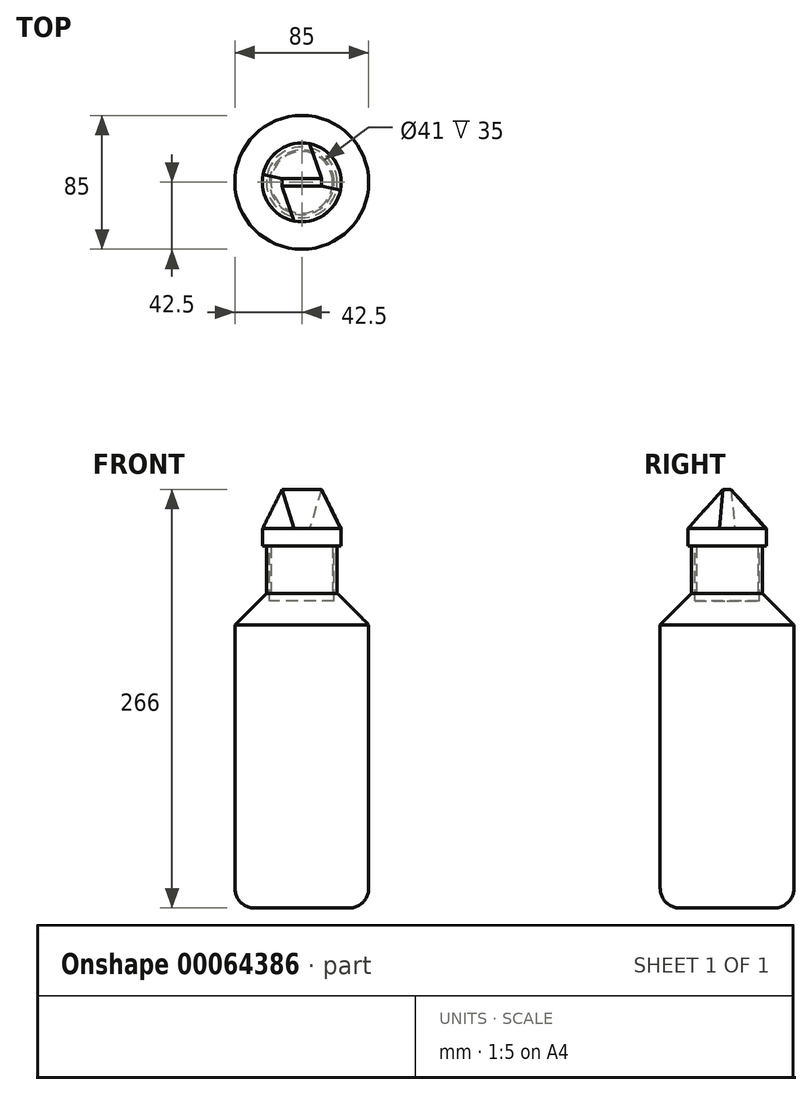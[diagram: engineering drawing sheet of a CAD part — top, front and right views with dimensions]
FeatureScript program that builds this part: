
annotation { "Feature Type Name" : "Feature", "Feature Type Description" : "" }
export const myFeature = defineFeature(function(context is Context, id is Id, definition is map)
    precondition{}
    {
        {
            var Q0;
            Q0=qCreatedBy(makeId("Top.planeOp"),FACE);
            var sketch = newSketch(context, id + "F0", { "sketchPlane" : qUnion([Q0])});
            skCircle(sketch, "E0", {"center": v(0, 0) * mm, "radius": 42.5 * mm});
            skSolve(sketch);
        }
        {
            var Q0;
            Q0 = qSketchRegion(id + "F0", true);
            extrude(context, id + "F1", {"entities" : qUnion([Q0]), "depth" : 180 * mm});
        }
        {
            var Q0;
            Q0=makeQuery(id+"F1.opExtrude","CAP_FACE",FACE,{"disambiguationData":[OSD([sQuery(id+"F0.wireOp",EDGE,"E0")])],"isStart":false});
            cPlane(context, id + "F2", {"entities" : qUnion([Q0]), "cplaneType" : CPlaneType.OFFSET, "offset" : 20 * mm, "width" : 152.4 * mm, "height" : 152.4 * mm});
        }
        {
            var Q0;
            Q0=qCreatedBy(id+"F2.planeOp",FACE);
            var sketch = newSketch(context, id + "F3", { "sketchPlane" : qUnion([Q0])});
            skCircle(sketch, "E1", {"center": v(0, 0) * mm, "radius": 22.5 * mm});
            skSolve(sketch);
        }
        {
            var Q1;
            Q1=makeQuery(id+"F1.opExtrude","CAP_FACE",FACE,{"disambiguationData":[OSD([sQuery(id+"F0.wireOp",EDGE,"E0")])],"isStart":false});
            var Q2;
            Q2=makeQuery(id+"F3.imprint","IMPRINT",FACE,{"disambiguationData":[TD([[makeQuery(id+"F3.imprint","IMPRINT",EDGE,{"derivedFrom":sQuery(id+"F3.wireOp",EDGE,"E1")}),1.0]])]});
            loft(context, id + "F4", {"operationType" : NewBodyOperationType.ADD, "sheetProfilesArray" : [{ "sheetProfileEntities" : qUnion([Q1]) }, { "sheetProfileEntities" : qUnion([Q2]) }]});
        }
        {
            var Q0;
            Q0=makeQuery(id+"F1.opExtrude","CAP_FACE",FACE,{"disambiguationData":[OSD([sQuery(id+"F0.wireOp",EDGE,"E0")])],"isStart":true});
            fillet(context, id + "F5", {"entities" : qUnion([Q0]), "radius" : 12.7 * mm, "tangentPropagation" : true, "allowEdgeOverflow" : false});
        }
        {
            var Q0;
            Q0=makeQuery(id+"F4.opLoft","CAP_FACE",FACE,{"disambiguationData":[OSD([makeQuery(id+"F3.imprint","IMPRINT",FACE,{"disambiguationData":[TD([[makeQuery(id+"F3.imprint","IMPRINT",EDGE,{"derivedFrom":sQuery(id+"F3.wireOp",EDGE,"E1")}),1.0]])]})])],"isStart":true});
            extrude(context, id + "F6", {"entities" : qUnion([Q0]), "operationType" : NewBodyOperationType.ADD, "depth" : 35 * mm});
        }
        {
            var Q0;
            Q0=makeQuery(id+"F6.opExtrude","CAP_FACE",FACE,{"disambiguationData":[OSD([makeQuery(id+"F3.imprint","IMPRINT",FACE,{"disambiguationData":[TD([[makeQuery(id+"F3.imprint","IMPRINT",EDGE,{"derivedFrom":sQuery(id+"F3.wireOp",EDGE,"E1")}),1.0]])]})])],"isStart":false});
            var sketch = newSketch(context, id + "F7", { "sketchPlane" : qUnion([Q0])});
            skCircle(sketch, "E2", {"center": v(0, 0) * mm, "radius": 20.5 * mm});
            skSolve(sketch);
        }
        {
            var Q0;
            Q0=makeQuery(id+"F7.imprint","IMPRINT",FACE,{"disambiguationData":[TD([[makeQuery(id+"F7.imprint","IMPRINT",EDGE,{"derivedFrom":sQuery(id+"F7.wireOp",EDGE,"E2")}),1.0]])]});
            extrude(context, id + "F8", {"entities" : qUnion([Q0]), "operationType" : NewBodyOperationType.REMOVE, "oppositeDirection" : true, "depth" : 40 * mm});
        }
        {
            var Q0;
            Q0=qCreatedBy(id+"F2.planeOp",FACE);
            var sketch = newSketch(context, id + "F9", { "sketchPlane" : qUnion([Q0])});
            skCircle(sketch, "E3", {"center": v(0, 0) * mm, "radius": 19.5 * mm});
            skSolve(sketch);
        }
        {
            var Q0;
            Q0 = qSketchRegion(id + "F9", true);
            extrude(context, id + "F10", {"entities" : qUnion([Q0]), "depth" : 30 * mm});
        }
        {
            var Q0;
            Q0=makeQuery(id+"F10.opExtrude","CAP_FACE",FACE,{"disambiguationData":[OSD([sQuery(id+"F9.wireOp",EDGE,"E3")])],"isStart":false});
            var sketch = newSketch(context, id + "F11", { "sketchPlane" : qUnion([Q0])});
            skCircle(sketch, "E4", {"center": v(0, 0) * mm, "radius": 25 * mm});
            skSolve(sketch);
        }
        {
            var Q0;
            Q0 = qSketchRegion(id + "F11", true);
            extrude(context, id + "F12", {"entities" : qUnion([Q0]), "operationType" : NewBodyOperationType.ADD, "depth" : 11 * mm});
        }
        {
            var Q0;
            Q0=makeQuery(id+"F12.opExtrude","CAP_FACE",FACE,{"disambiguationData":[OSD([sQuery(id+"F11.wireOp",EDGE,"E4")])],"isStart":false});
            cPlane(context, id + "F13", {"entities" : qUnion([Q0]), "cplaneType" : CPlaneType.OFFSET, "offset" : 25 * mm, "width" : 152.4 * mm, "height" : 152.4 * mm});
        }
        {
            var Q0;
            Q0=qCreatedBy(id+"F13.planeOp",FACE);
            var sketch = newSketch(context, id + "F14", { "sketchPlane" : qUnion([Q0])});
            skLineSegment(sketch, "E5.rect.bottom", {"start": v(12.5, -2.5) * mm, "end": v(-12.5, -2.5) * mm});
            skLineSegment(sketch, "E5.rect.top", {"start": v(12.5, 2.5) * mm, "end": v(-12.5, 2.5) * mm});
            skLineSegment(sketch, "E5.rect.left", {"start": v(12.5, -2.5) * mm, "end": v(12.5, 2.5) * mm});
            skLineSegment(sketch, "E5.rect.right", {"start": v(-12.5, -2.5) * mm, "end": v(-12.5, 2.5) * mm});
            skPoint(sketch, "E5.rect.middle", {"position": v(0, 0) * mm});
            skSolve(sketch);
        }
        {
            var Q0;
            Q0=makeQuery(id+"F14.imprint","IMPRINT",FACE,{"disambiguationData":[TD([[makeQuery(id+"F14.imprint","IMPRINT",EDGE,{"derivedFrom":sQuery(id+"F14.wireOp",EDGE,"E5.rect.bottom")}),-1.0]])]});
            var Q1;
            Q1=makeQuery(id+"F12.opExtrude","CAP_FACE",FACE,{"disambiguationData":[OSD([sQuery(id+"F11.wireOp",EDGE,"E4")])],"isStart":false});
            loft(context, id + "F15", {"sheetProfilesArray" : [{ "sheetProfileEntities" : qUnion([Q0]) }, { "sheetProfileEntities" : qUnion([Q1]) }]});
        }
    });
